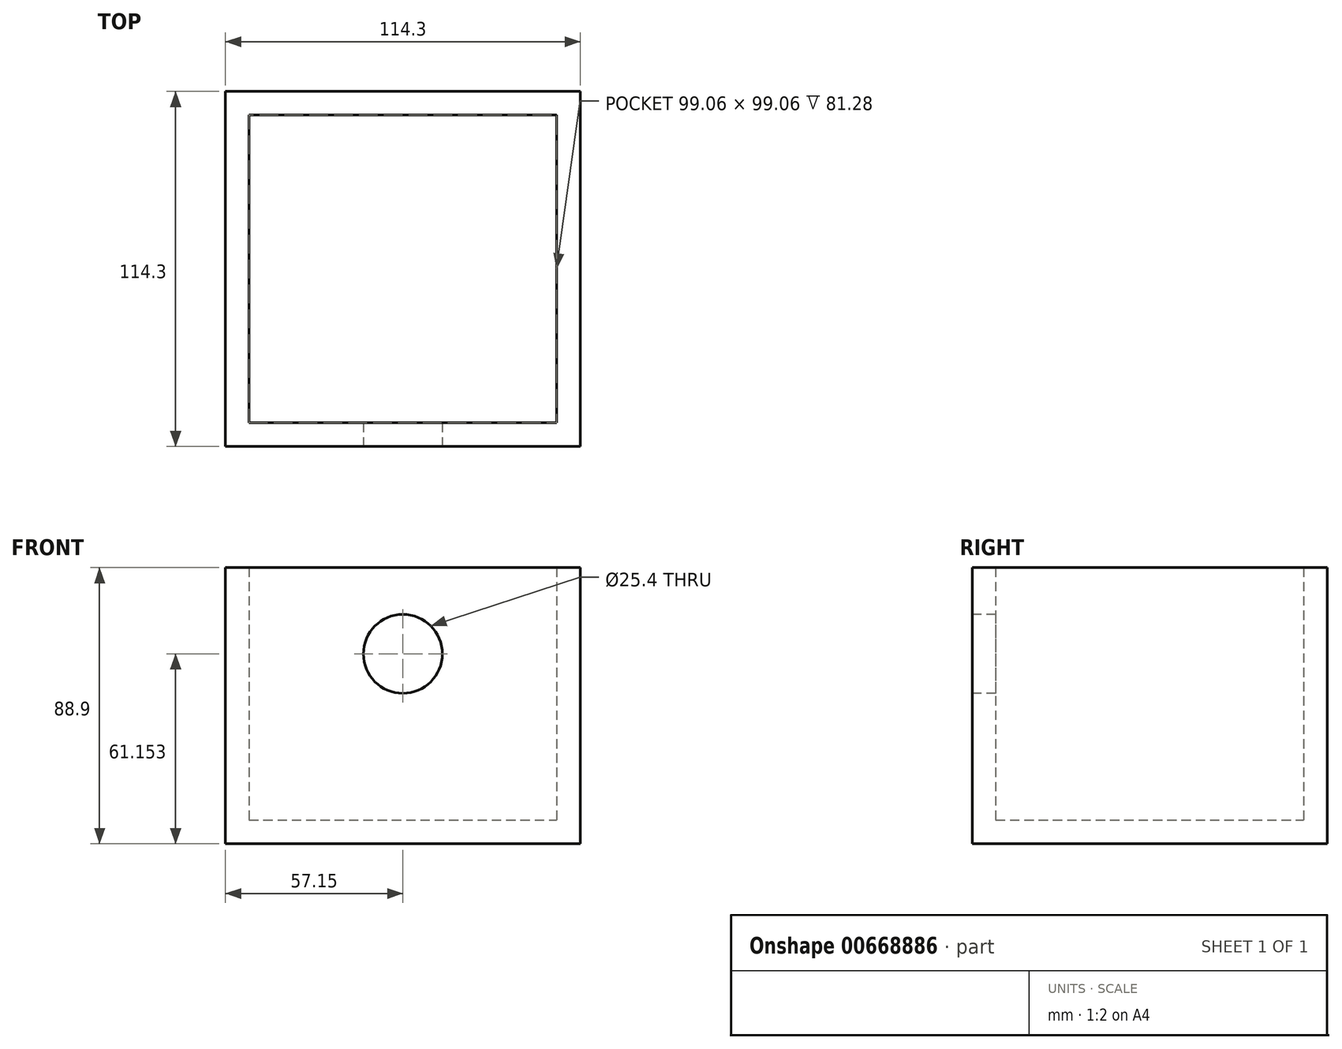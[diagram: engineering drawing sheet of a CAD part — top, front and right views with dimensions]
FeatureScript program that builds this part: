
annotation { "Feature Type Name" : "Feature", "Feature Type Description" : "" }
export const myFeature = defineFeature(function(context is Context, id is Id, definition is map)
    precondition{}
    {
        {
            var Q0;
            Q0=qCreatedBy(makeId("Top.planeOp"),FACE);
            var sketch = newSketch(context, id + "F0", { "sketchPlane" : qUnion([Q0])});
            skLineSegment(sketch, "E0.bottom", {"start": v(-57.15, -57.15) * mm, "end": v(57.15, -57.15) * mm});
            skLineSegment(sketch, "E0.top", {"start": v(-57.15, 57.15) * mm, "end": v(57.15, 57.15) * mm});
            skLineSegment(sketch, "E0.left", {"start": v(-57.15, -57.15) * mm, "end": v(-57.15, 57.15) * mm});
            skLineSegment(sketch, "E0.right", {"start": v(57.15, -57.15) * mm, "end": v(57.15, 57.15) * mm});
            skPoint(sketch, "E0.middle", {"position": v(0, 0) * mm});
            skLineSegment(sketch, "E1.0", {"start": v(49.53, -49.53) * mm, "end": v(49.53, 49.53) * mm});
            skLineSegment(sketch, "E1.1", {"start": v(-49.53, -49.53) * mm, "end": v(49.53, -49.53) * mm});
            skLineSegment(sketch, "E1.2", {"start": v(-49.53, -49.53) * mm, "end": v(-49.53, 49.53) * mm});
            skLineSegment(sketch, "E1.3", {"start": v(-49.53, 49.53) * mm, "end": v(49.53, 49.53) * mm});
            skSolve(sketch);
        }
        {
            var Q0;
            Q0=makeQuery(id+"F0.imprint","IMPRINT",FACE,{"disambiguationData":[TD([[makeQuery(id+"F0.imprint","IMPRINT",EDGE,{"derivedFrom":sQuery(id+"F0.wireOp",EDGE,"E1.0")}),1.0]])]});
            extrude(context, id + "F1", {"entities" : qUnion([Q0]), "depth" : 7.62 * mm, "offsetDistance" : 25.4 * mm});
        }
        {
            var Q0;
            Q0=makeQuery(id+"F0.imprint","IMPRINT",FACE,{"disambiguationData":[TD([[makeQuery(id+"F0.imprint","IMPRINT",EDGE,{"derivedFrom":sQuery(id+"F0.wireOp",EDGE,"E0.bottom")}),1.0]])]});
            extrude(context, id + "F2", {"entities" : qUnion([Q0]), "operationType" : NewBodyOperationType.ADD, "depth" : 88.9 * mm, "offsetDistance" : 25.4 * mm});
        }
        {
            var Q0;
            Q0=makeQuery(id+"F2.opExtrude","SWEPT_FACE",FACE,{"disambiguationData":[OSD([sQuery(id+"F0.wireOp",EDGE,"E0.bottom")])]});
            var sketch = newSketch(context, id + "F3", { "sketchPlane" : qUnion([Q0])});
            skCircle(sketch, "E2", {"center": v(0, 61.15) * mm, "radius": 12.7 * mm});
            skSolve(sketch);
        }
        {
            var Q0;
            Q0=makeQuery(id+"F3.imprint","IMPRINT",FACE,{"disambiguationData":[TD([[makeQuery(id+"F3.imprint","IMPRINT",EDGE,{"derivedFrom":sQuery(id+"F3.wireOp",EDGE,"E2")}),1.0]])]});
            extrude(context, id + "F4", {"entities" : qUnion([Q0]), "operationType" : NewBodyOperationType.REMOVE, "oppositeDirection" : true, "depth" : 19.13 * mm, "offsetDistance" : 25.4 * mm});
        }
    });
